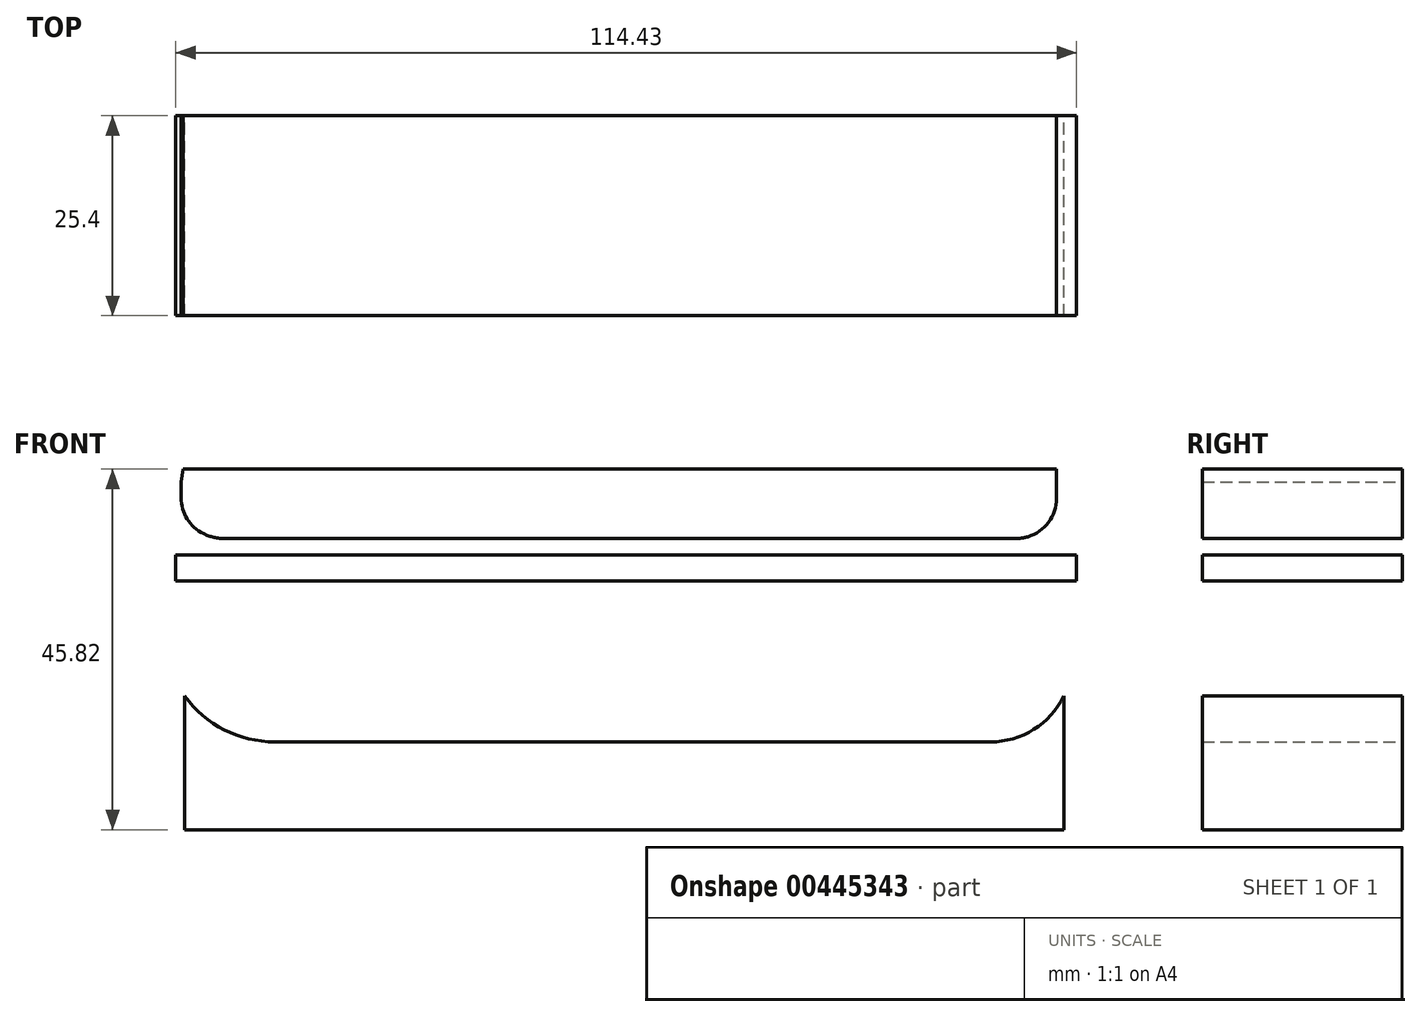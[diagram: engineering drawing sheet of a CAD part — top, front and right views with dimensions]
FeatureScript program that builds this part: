
annotation { "Feature Type Name" : "Feature", "Feature Type Description" : "" }
export const myFeature = defineFeature(function(context is Context, id is Id, definition is map)
    precondition{}
    {
        {
            var Q0;
            Q0=qCreatedBy(makeId("Front.planeOp"),FACE);
            var sketch = newSketch(context, id + "F0", { "sketchPlane" : qUnion([Q0])});
            skLineSegment(sketch, "E0", {"start": v(-51.4, 16.98) * mm, "end": v(-51.4, 0) * mm});
            skLineSegment(sketch, "E1", {"start": v(-51.4, 0) * mm, "end": v(60.24, 0) * mm});
            skLineSegment(sketch, "E2", {"start": v(60.24, 0) * mm, "end": v(60.24, 16.98) * mm});
            skLineSegment(sketch, "E3", {"start": v(-40, 11.16) * mm, "end": v(50.94, 11.16) * mm});
            skArc(sketch, "E4", {"start": v(-51.4, 16.98) * mm, "mid": v(-46.4, 12.7) * mm, "end": v(-40, 11.16) * mm});
            skArc(sketch, "E5", {"start": v(50.94, 11.16) * mm, "mid": v(56.42, 12.74) * mm, "end": v(60.24, 16.98) * mm});
            skLineSegment(sketch, "E6.bottom", {"start": v(-52.56, 34.89) * mm, "end": v(61.87, 34.89) * mm});
            skLineSegment(sketch, "E6.top", {"start": v(-52.56, 31.63) * mm, "end": v(61.87, 31.63) * mm});
            skLineSegment(sketch, "E6.left", {"start": v(-52.56, 34.89) * mm, "end": v(-52.56, 31.63) * mm});
            skLineSegment(sketch, "E6.right", {"start": v(61.87, 34.89) * mm, "end": v(61.87, 31.63) * mm});
            skLineSegment(sketch, "E7", {"start": v(-51.87, 44.2) * mm, "end": v(-51.87, 40.47) * mm});
            skLineSegment(sketch, "E8", {"start": v(-46.28, 36.98) * mm, "end": v(53.96, 36.98) * mm});
            skLineSegment(sketch, "E9", {"start": v(59.3, 40.24) * mm, "end": v(59.3, 45.82) * mm});
            skLineSegment(sketch, "E10", {"start": v(59.3, 45.82) * mm, "end": v(-51.63, 45.82) * mm});
            skLineSegment(sketch, "E11", {"start": v(-51.63, 45.82) * mm, "end": v(-51.87, 44.2) * mm});
            skArc(sketch, "E12", {"start": v(-51.87, 40.47) * mm, "mid": v(-49.58, 37.93) * mm, "end": v(-46.28, 36.98) * mm});
            skArc(sketch, "E13", {"start": v(53.96, 36.98) * mm, "mid": v(57.1, 37.86) * mm, "end": v(59.3, 40.24) * mm});
            skSolve(sketch);
        }
        {
            var Q0;
            Q0=makeQuery(id+"F0.imprint","IMPRINT",FACE,{"disambiguationData":[TD([[makeQuery(id+"F0.imprint","IMPRINT",EDGE,{"derivedFrom":sQuery(id+"F0.wireOp",EDGE,"E7")}),1.0]])]});
            var Q1;
            Q1=makeQuery(id+"F0.imprint","IMPRINT",FACE,{"disambiguationData":[TD([[makeQuery(id+"F0.imprint","IMPRINT",EDGE,{"derivedFrom":sQuery(id+"F0.wireOp",EDGE,"E6.bottom")}),-1.0]])]});
            var Q2;
            Q2=makeQuery(id+"F0.imprint","IMPRINT",FACE,{"disambiguationData":[TD([[makeQuery(id+"F0.imprint","IMPRINT",EDGE,{"derivedFrom":sQuery(id+"F0.wireOp",EDGE,"E0")}),1.0]])]});
            extrude(context, id + "F1", {"entities" : qUnion([Q0, Q1, Q2]), "depth" : 25.4 * mm});
        }
        {
            var Q0;
            Q0=makeQuery(id+"F1.opExtrude","SWEPT_EDGE",EDGE,{"disambiguationData":[OSD([sQuery(id+"F0.wireOp",EDGE,"E7"),sQuery(id+"F0.wireOp",EDGE,"E12")])]});
            fillet(context, id + "F2", {"entities" : qUnion([Q0]), "radius" : 5.08 * mm, "tangentPropagation" : true, "allowEdgeOverflow" : false});
        }
        {
            var Q0;
            Q0=makeQuery(id+"F1.opExtrude","SWEPT_EDGE",EDGE,{"disambiguationData":[OSD([sQuery(id+"F0.wireOp",EDGE,"E9"),sQuery(id+"F0.wireOp",EDGE,"E13")])]});
            fillet(context, id + "F3", {"entities" : qUnion([Q0]), "radius" : 5.08 * mm, "tangentPropagation" : true, "allowEdgeOverflow" : false});
        }
    });
